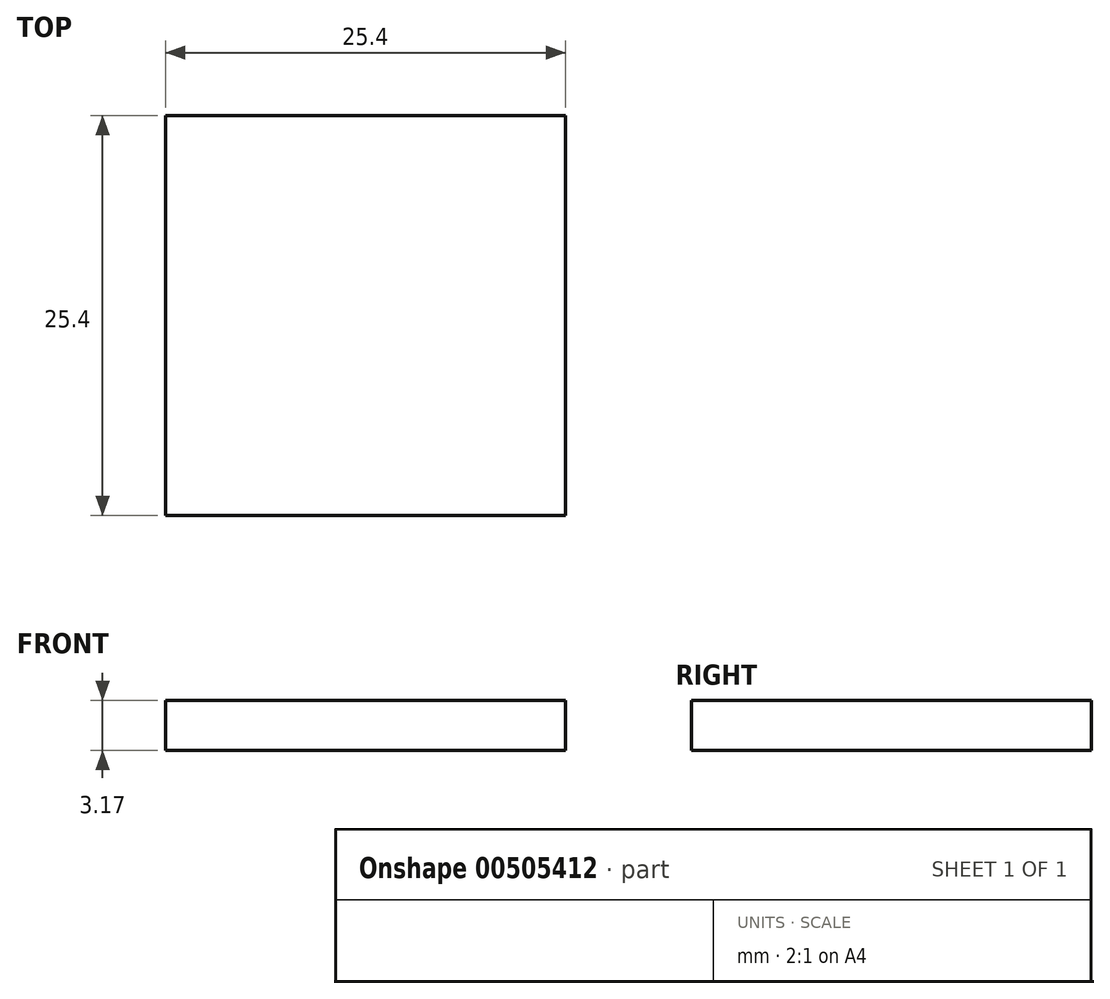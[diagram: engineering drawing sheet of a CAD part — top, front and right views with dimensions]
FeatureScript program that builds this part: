
annotation { "Feature Type Name" : "Feature", "Feature Type Description" : "" }
export const myFeature = defineFeature(function(context is Context, id is Id, definition is map)
    precondition{}
    {
        {
            var Q0;
            Q0=qCreatedBy(makeId("Top.planeOp"),FACE);
            var sketch = newSketch(context, id + "F0", { "sketchPlane" : qUnion([Q0])});
            skLineSegment(sketch, "E0.bottom", {"start": v(-12.7, 12.7) * mm, "end": v(12.7, 12.7) * mm});
            skLineSegment(sketch, "E0.top", {"start": v(-12.7, -12.7) * mm, "end": v(12.7, -12.7) * mm});
            skLineSegment(sketch, "E0.left", {"start": v(-12.7, 12.7) * mm, "end": v(-12.7, -12.7) * mm});
            skLineSegment(sketch, "E0.right", {"start": v(12.7, 12.7) * mm, "end": v(12.7, -12.7) * mm});
            skPoint(sketch, "E0.middle", {"position": v(0, 0) * mm});
            skSolve(sketch);
        }
        {
            var Q0;
            Q0=makeQuery(id+"F0.imprint","IMPRINT",FACE,{"disambiguationData":[TD([[makeQuery(id+"F0.imprint","IMPRINT",EDGE,{"derivedFrom":sQuery(id+"F0.wireOp",EDGE,"E0.bottom")}),-1.0]])]});
            extrude(context, id + "F1", {"entities" : qUnion([Q0]), "depth" : 3.17 * mm, "offsetDistance" : 25.4 * mm});
        }
    });
